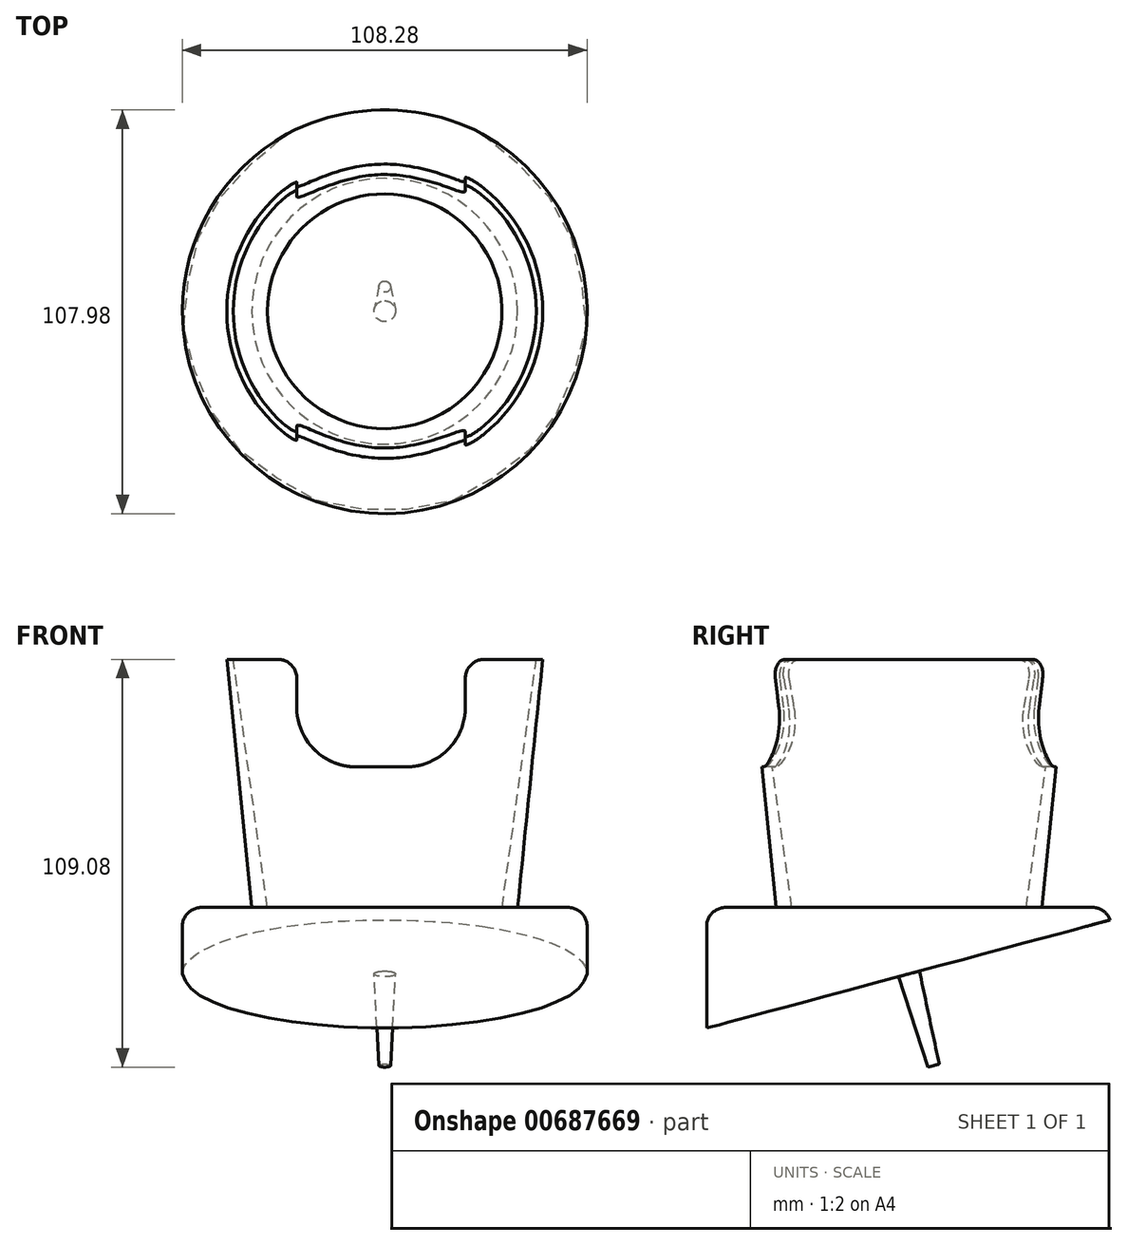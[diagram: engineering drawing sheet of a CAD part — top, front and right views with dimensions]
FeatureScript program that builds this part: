
annotation { "Feature Type Name" : "Feature", "Feature Type Description" : "" }
export const myFeature = defineFeature(function(context is Context, id is Id, definition is map)
    precondition{}
    {
        {
            var Q0;
            Q0=qCreatedBy(makeId("Front.planeOp"),FACE);
            var sketch = newSketch(context, id + "F0", { "sketchPlane" : qUnion([Q0])});
            skLineSegment(sketch, "E0", {"start": v(-35.56, 0) * mm, "end": v(-42.26, 66.36) * mm});
            skLineSegment(sketch, "E1", {"start": v(-42.26, 66.36) * mm, "end": v(0, 66.36) * mm});
            skLineSegment(sketch, "E2", {"start": v(0, 66.36) * mm, "end": v(0, 0) * mm});
            skLineSegment(sketch, "E3", {"start": v(0, 0) * mm, "end": v(-35.56, 0) * mm});
            skSolve(sketch);
        }
        {
            var Q0;
            Q0 = qSketchRegion(id + "F0", true);
            var Q1;
            Q1=sQuery(id+"F0.wireOp",EDGE,"E2");
            revolve(context, id + "F1", {"entities" : qUnion([Q0]), "axis" : qUnion([Q1]), "revolveType" : RevolveType.FULL});
        }
        {
            var Q0;
            Q0=qCreatedBy(makeId("Front.planeOp"),FACE);
            var sketch = newSketch(context, id + "F2", { "sketchPlane" : qUnion([Q0])});
            skLineSegment(sketch, "E4", {"start": v(0, 0) * mm, "end": v(-31.4, 0) * mm});
            skLineSegment(sketch, "E5", {"start": v(-31.4, 0) * mm, "end": v(-40.84, 68.58) * mm});
            skLineSegment(sketch, "E6", {"start": v(-40.84, 68.58) * mm, "end": v(0, 68.58) * mm});
            skLineSegment(sketch, "E7", {"start": v(0, 68.58) * mm, "end": v(0, 0) * mm});
            skSolve(sketch);
        }
        {
            var Q0;
            Q0 = qSketchRegion(id + "F2", true);
            var Q1;
            Q1=sQuery(id+"F2.wireOp",EDGE,"E7");
            revolve(context, id + "F3", {"operationType" : NewBodyOperationType.REMOVE, "entities" : qUnion([Q0]), "axis" : qUnion([Q1]), "revolveType" : RevolveType.FULL, "oppositeDirection" : true});
        }
        {
            var Q0;
            Q0=qCreatedBy(makeId("Front.planeOp"),FACE);
            var sketch = newSketch(context, id + "F4", { "sketchPlane" : qUnion([Q0])});
            skLineSegment(sketch, "E8.bottom", {"start": v(-23.52, 66.53) * mm, "end": v(21.55, 66.53) * mm});
            skLineSegment(sketch, "E8.top", {"start": v(-23.52, 37.6) * mm, "end": v(21.55, 37.6) * mm});
            skLineSegment(sketch, "E8.left", {"start": v(-23.52, 66.53) * mm, "end": v(-23.52, 37.6) * mm});
            skLineSegment(sketch, "E8.right", {"start": v(21.55, 66.53) * mm, "end": v(21.55, 37.6) * mm});
            skSolve(sketch);
        }
        {
            var Q0;
            Q0 = qSketchRegion(id + "F4", true);
            extrude(context, id + "F5", {"entities" : qUnion([Q0]), "operationType" : NewBodyOperationType.REMOVE, "endBound" : BoundingType.SYMMETRIC, "oppositeDirection" : true, "depth" : 152.4 * mm, "offsetDistance" : 25.4 * mm});
        }
        {
            var Q0;
            Q0=makeQuery(id+"F5.boolean.opBoolean","COPY",EDGE,{"disambiguationData":[OD(0.0)],"derivedFrom":makeQuery(id+"F5.opExtrude","SWEPT_EDGE",EDGE,{"disambiguationData":[OSD([sQuery(id+"F4.wireOp",EDGE,"E8.top"),sQuery(id+"F4.wireOp",EDGE,"E8.left")])]})});
            var Q1;
            Q1=makeQuery(id+"F5.boolean.opBoolean","COPY",EDGE,{"disambiguationData":[OD(0.0)],"derivedFrom":makeQuery(id+"F5.opExtrude","SWEPT_EDGE",EDGE,{"disambiguationData":[OSD([sQuery(id+"F4.wireOp",EDGE,"E8.top"),sQuery(id+"F4.wireOp",EDGE,"E8.right")])]})});
            var Q2;
            Q2=makeQuery(id+"F5.boolean.opBoolean","COPY",EDGE,{"disambiguationData":[OD(1.0)],"derivedFrom":makeQuery(id+"F5.opExtrude","SWEPT_EDGE",EDGE,{"disambiguationData":[OSD([sQuery(id+"F4.wireOp",EDGE,"E8.top"),sQuery(id+"F4.wireOp",EDGE,"E8.left")])]})});
            var Q3;
            Q3=makeQuery(id+"F5.boolean.opBoolean","COPY",EDGE,{"disambiguationData":[OD(1.0)],"derivedFrom":makeQuery(id+"F5.opExtrude","SWEPT_EDGE",EDGE,{"disambiguationData":[OSD([sQuery(id+"F4.wireOp",EDGE,"E8.top"),sQuery(id+"F4.wireOp",EDGE,"E8.right")])]})});
            fillet(context, id + "F6", {"entities" : qUnion([Q0, Q1, Q2, Q3]), "radius" : 15.88 * mm, "tangentPropagation" : true, "allowEdgeOverflow" : false});
        }
        {
            var Q0;
            Q0=makeQuery(id+"F5.boolean.opBoolean","INTERSECT",EDGE,{"disambiguationData":[OD(0.0)],"derivedFrom":[makeQuery(id+"F1.opRevolve","SWEPT_FACE",FACE,{"disambiguationData":[OSD([sQuery(id+"F0.wireOp",EDGE,"E1")])]}),makeQuery(id+"F5.opExtrude","SWEPT_FACE",FACE,{"disambiguationData":[OSD([sQuery(id+"F4.wireOp",EDGE,"E8.left")])]})]});
            var Q1;
            Q1=makeQuery(id+"F5.boolean.opBoolean","INTERSECT",EDGE,{"disambiguationData":[OD(0.0)],"derivedFrom":[makeQuery(id+"F1.opRevolve","SWEPT_FACE",FACE,{"disambiguationData":[OSD([sQuery(id+"F0.wireOp",EDGE,"E1")])]}),makeQuery(id+"F5.opExtrude","SWEPT_FACE",FACE,{"disambiguationData":[OSD([sQuery(id+"F4.wireOp",EDGE,"E8.right")])]})]});
            var Q2;
            Q2=makeQuery(id+"F5.boolean.opBoolean","INTERSECT",EDGE,{"disambiguationData":[OD(1.0)],"derivedFrom":[makeQuery(id+"F1.opRevolve","SWEPT_FACE",FACE,{"disambiguationData":[OSD([sQuery(id+"F0.wireOp",EDGE,"E1")])]}),makeQuery(id+"F5.opExtrude","SWEPT_FACE",FACE,{"disambiguationData":[OSD([sQuery(id+"F4.wireOp",EDGE,"E8.right")])]})]});
            var Q3;
            Q3=makeQuery(id+"F5.boolean.opBoolean","INTERSECT",EDGE,{"disambiguationData":[OD(1.0)],"derivedFrom":[makeQuery(id+"F1.opRevolve","SWEPT_FACE",FACE,{"disambiguationData":[OSD([sQuery(id+"F0.wireOp",EDGE,"E1")])]}),makeQuery(id+"F5.opExtrude","SWEPT_FACE",FACE,{"disambiguationData":[OSD([sQuery(id+"F4.wireOp",EDGE,"E8.left")])]})]});
            fillet(context, id + "F7", {"entities" : qUnion([Q0, Q1, Q2, Q3]), "radius" : 5.08 * mm, "tangentPropagation" : true, "allowEdgeOverflow" : false});
        }
        {
            var Q0;
            Q0=qCreatedBy(makeId("Right.planeOp"),FACE);
            var sketch = newSketch(context, id + "F8", { "sketchPlane" : qUnion([Q0])});
            skLineSegment(sketch, "E9.bottom", {"start": v(54.14, 0) * mm, "end": v(0, 0) * mm});
            skLineSegment(sketch, "E9.top", {"start": v(54.14, -50.8) * mm, "end": v(0, -50.8) * mm});
            skLineSegment(sketch, "E9.left", {"start": v(54.14, 0) * mm, "end": v(54.14, -50.8) * mm});
            skLineSegment(sketch, "E9.right", {"start": v(0, 0) * mm, "end": v(0, -50.8) * mm});
            skSolve(sketch);
        }
        {
            var Q0;
            Q0 = qSketchRegion(id + "F8", true);
            var Q1;
            Q1=sQuery(id+"F8.wireOp",EDGE,"E9.right");
            revolve(context, id + "F9", {"operationType" : NewBodyOperationType.ADD, "entities" : qUnion([Q0]), "axis" : qUnion([Q1]), "revolveType" : RevolveType.FULL});
        }
        {
            var Q0;
            Q0=qCreatedBy(makeId("Right.planeOp"),FACE);
            var sketch = newSketch(context, id + "F10", { "sketchPlane" : qUnion([Q0])});
            skLineSegment(sketch, "E10", {"start": v(-55.36, -32.61) * mm, "end": v(58.21, -2.18) * mm});
            skLineSegment(sketch, "E11", {"start": v(-55.36, -32.61) * mm, "end": v(-55.36, -56.32) * mm});
            skLineSegment(sketch, "E12", {"start": v(-55.36, -56.32) * mm, "end": v(58.21, -56.32) * mm});
            skLineSegment(sketch, "E13", {"start": v(58.21, -56.32) * mm, "end": v(58.21, -2.18) * mm});
            skSolve(sketch);
        }
        {
            var Q0;
            Q0 = qSketchRegion(id + "F10", true);
            extrude(context, id + "F11", {"entities" : qUnion([Q0]), "operationType" : NewBodyOperationType.REMOVE, "endBound" : BoundingType.SYMMETRIC, "oppositeDirection" : true, "depth" : 203.2 * mm, "offsetDistance" : 25.4 * mm});
        }
        {
            var Q0;
            Q0=makeQuery(id+"F9.opRevolve","SWEPT_EDGE",EDGE,{"disambiguationData":[OSD([sQuery(id+"F8.wireOp",EDGE,"E9.bottom"),sQuery(id+"F8.wireOp",EDGE,"E9.left")])]});
            fillet(context, id + "F12", {"entities" : qUnion([Q0]), "radius" : 5.08 * mm, "tangentPropagation" : true, "allowEdgeOverflow" : false});
        }
        {
            var Q0;
            Q0=makeQuery(id+"F11.boolean.opBoolean","COPY",FACE,{"derivedFrom":makeQuery(id+"F11.opExtrude","SWEPT_FACE",FACE,{"disambiguationData":[OSD([sQuery(id+"F10.wireOp",EDGE,"E10")])]})});
            var sketch = newSketch(context, id + "F13", { "sketchPlane" : qUnion([Q0])});
            skCircle(sketch, "E14", {"center": v(0, 4.6) * mm, "radius": 4.1 * mm});
            skSolve(sketch);
        }
        {
            var Q0;
            Q0=makeQuery(id+"F13.imprint","IMPRINT",FACE,{"disambiguationData":[TD([[makeQuery(id+"F13.imprint","IMPRINT",EDGE,{"derivedFrom":sQuery(id+"F13.wireOp",EDGE,"E14")}),1.0]])]});
            var Q1;
            Q1=sQuery(id+"F13.wireOp",EDGE,"E14");
            extrude(context, id + "F14", {"entities" : qUnion([Q0]), "operationType" : NewBodyOperationType.ADD, "surfaceEntities" : qUnion([Q1]), "depth" : 25.4 * mm, "offsetDistance" : 25.4 * mm});
        }
        {
            var Q0;
            Q0=makeQuery(id+"F14.opExtrude","CAP_EDGE",EDGE,{"disambiguationData":[OSD([sQuery(id+"F13.wireOp",EDGE,"E14")])],"isStart":false});
            chamfer(context, id + "F15", {"entities" : qUnion([Q0]), "chamferType" : ChamferType.OFFSET_ANGLE, "width" : 2.54 * mm, "oppositeDirection" : false, "angle" : 87 * degree, "tangentPropagation" : true});
        }
    });
